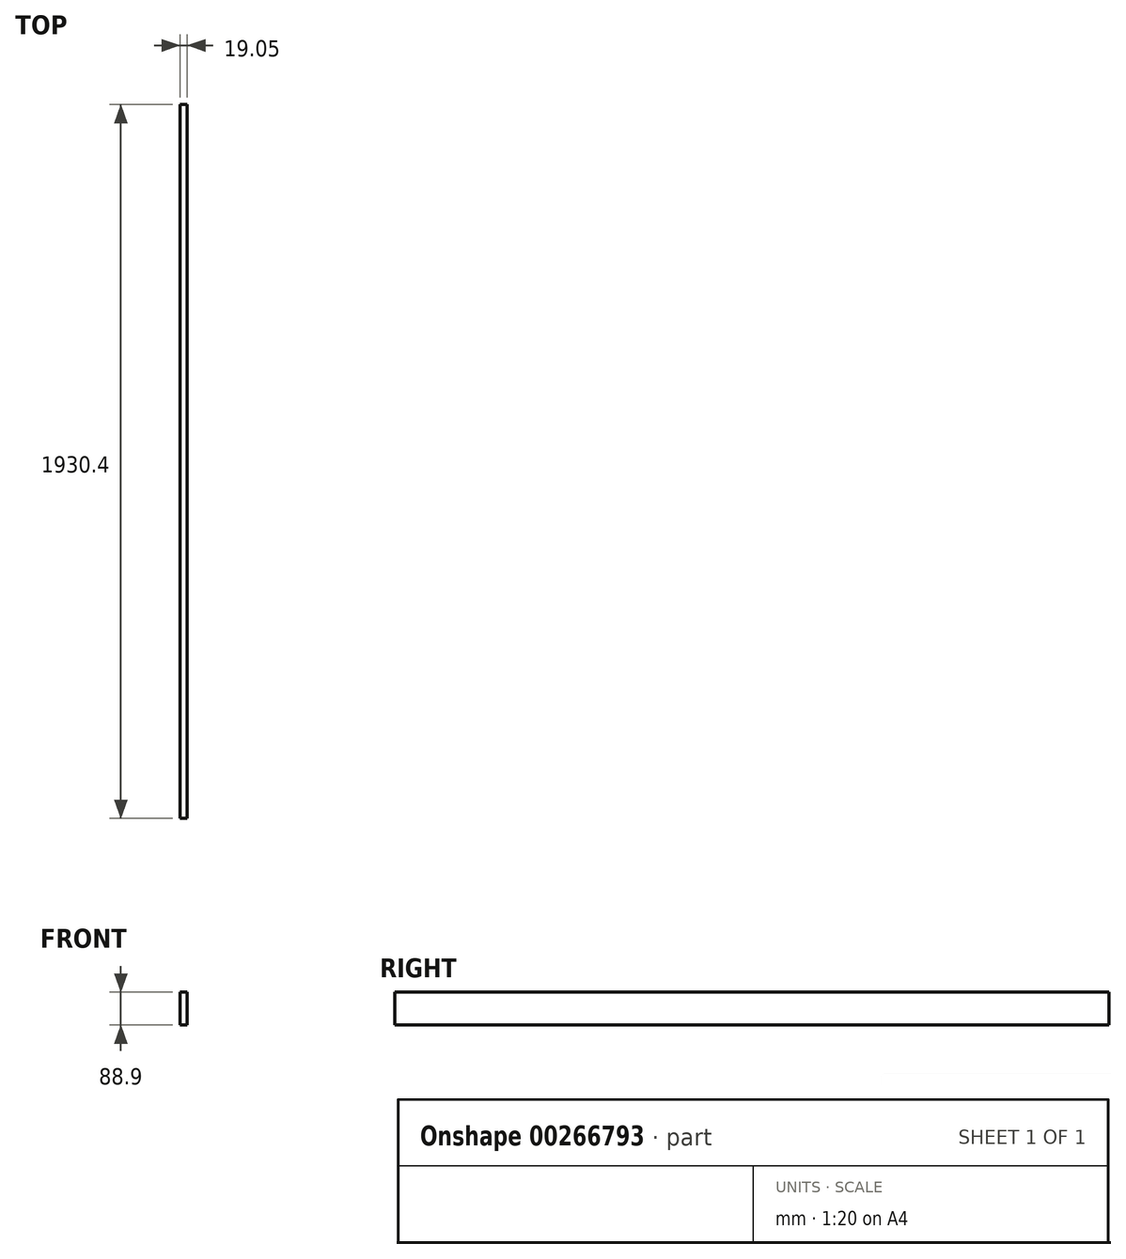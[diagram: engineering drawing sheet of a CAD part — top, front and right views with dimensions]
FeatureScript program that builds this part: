
annotation { "Feature Type Name" : "Feature", "Feature Type Description" : "" }
export const myFeature = defineFeature(function(context is Context, id is Id, definition is map)
    precondition{}
    {
        {
            var Q0;
            Q0=qCreatedBy(makeId("Front.planeOp"),FACE);
            var sketch = newSketch(context, id + "F0", { "sketchPlane" : qUnion([Q0])});
            skLineSegment(sketch, "E0.bottom", {"start": v(-48.34, 74.48) * mm, "end": v(-29.3, 74.48) * mm});
            skLineSegment(sketch, "E0.top", {"start": v(-48.34, -14.42) * mm, "end": v(-29.3, -14.42) * mm});
            skLineSegment(sketch, "E0.left", {"start": v(-48.34, 74.48) * mm, "end": v(-48.34, -14.42) * mm});
            skLineSegment(sketch, "E0.right", {"start": v(-29.3, 74.48) * mm, "end": v(-29.3, -14.42) * mm});
            skSolve(sketch);
        }
        {
            var Q0;
            Q0=qSketchRegion(id+"F0",true);
            extrude(context, id + "F1", {"entities" : qUnion([Q0]), "depth" : 1930.4 * mm});
        }
    });
